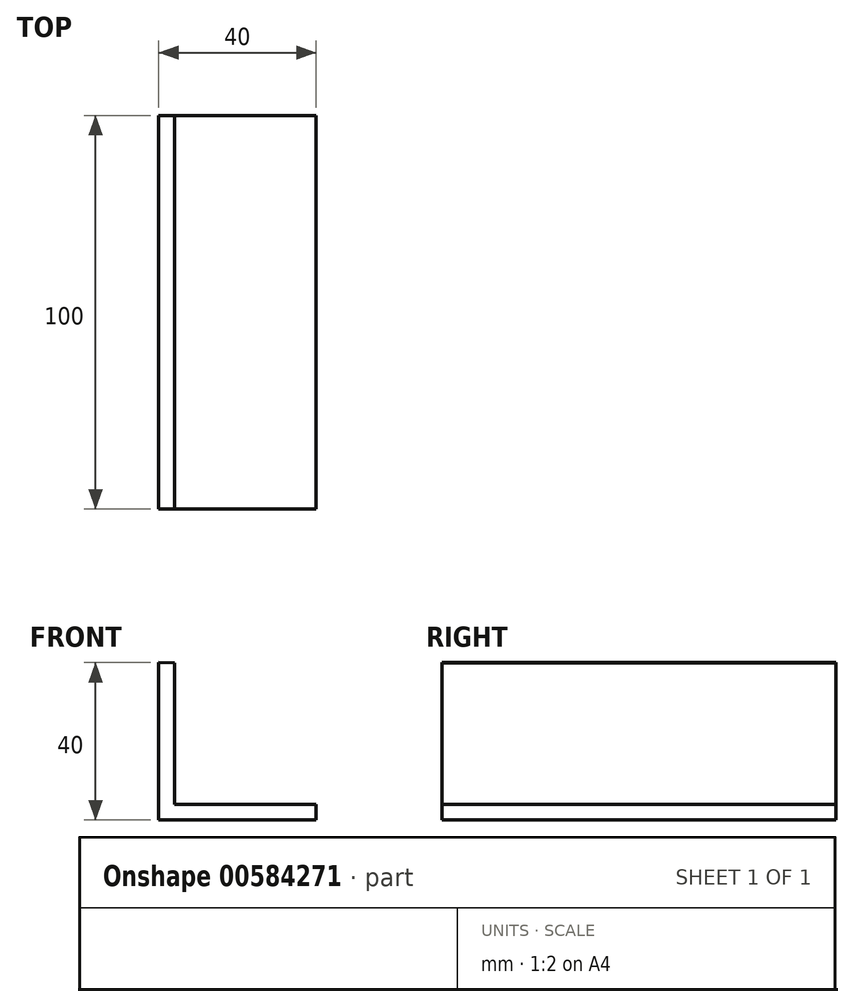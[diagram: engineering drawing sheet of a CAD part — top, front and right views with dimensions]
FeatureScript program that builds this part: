
annotation { "Feature Type Name" : "Feature", "Feature Type Description" : "" }
export const myFeature = defineFeature(function(context is Context, id is Id, definition is map)
    precondition{}
    {
        {
            var Q0;
            Q0=qCreatedBy(makeId("Front.planeOp"),FACE);
            var sketch = newSketch(context, id + "F0", { "sketchPlane" : qUnion([Q0])});
            skLineSegment(sketch, "E0", {"start": v(8.14, 23.7) * mm, "end": v(8.14, -16.3) * mm});
            skLineSegment(sketch, "E1", {"start": v(8.14, -16.3) * mm, "end": v(48.14, -16.3) * mm});
            skLineSegment(sketch, "E2", {"start": v(48.14, -16.3) * mm, "end": v(48.14, -12.3) * mm});
            skLineSegment(sketch, "E3", {"start": v(48.14, -12.3) * mm, "end": v(12.14, -12.3) * mm});
            skLineSegment(sketch, "E4", {"start": v(12.14, -12.3) * mm, "end": v(12.14, 23.64) * mm});
            skLineSegment(sketch, "E5", {"start": v(12.14, 23.64) * mm, "end": v(8.14, 23.7) * mm});
            skSolve(sketch);
        }
        {
            var Q0;
            Q0=makeQuery(id+"F0.imprint","IMPRINT",FACE,{"disambiguationData":[TD([[makeQuery(id+"F0.imprint","IMPRINT",EDGE,{"derivedFrom":sQuery(id+"F0.wireOp",EDGE,"E0")}),1.0]])]});
            extrude(context, id + "F1", {"entities" : qUnion([Q0]), "depth" : 100 * mm, "offsetDistance" : 25 * mm});
        }
    });
